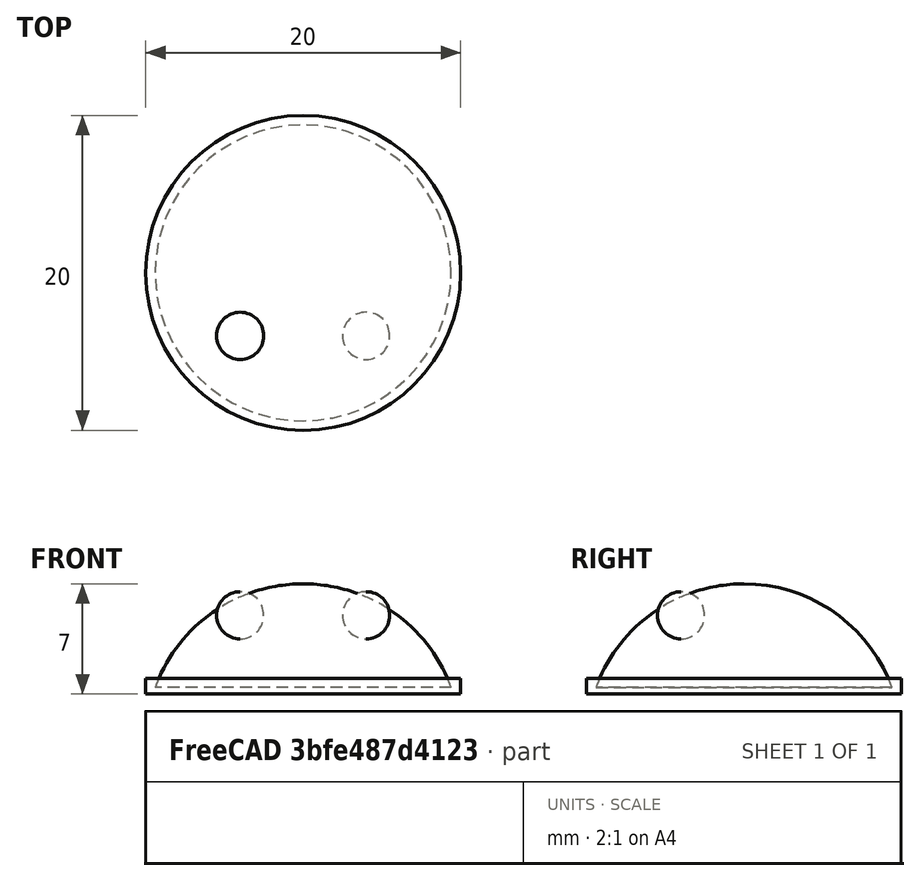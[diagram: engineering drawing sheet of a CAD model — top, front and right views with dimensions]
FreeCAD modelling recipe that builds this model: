
FCSTD DOCUMENT  (FreeCAD 0.21R33694 (Git))
Label: OJT1_T13R01_capderobot
License: All rights reserved
LicenseURL: https://en.wikipedia.org/wiki/All_rights_reserved
objects: Part::Sphere×3, Part::Cylinder×1
note: 4 computed .brp shape members not serialized (recipe doc carries the construction recipe); baked Part::Feature solids carry a one-line shape summary decoded from their .brp

FEATURE [Part::Cylinder] Cylinder  label="Cilindre"
  Angle = 360
  AttacherType = Attacher::AttachEngine3D
  FirstAngle = 0
  Height = 1
  Radius = 10
  SecondAngle = 0
FEATURE [Part::Sphere] Sphere  label="Esfera"
  Angle1 = 20
  Angle2 = 90
  Angle3 = 360
  AttacherType = Attacher::AttachEngine3D
  Placement = pos=(0,0,-3) rot=(0,0,1;0rad)
  Radius = 10
FEATURE [Part::Sphere] Sphere001  label="Ull_1"
  Angle1 = -90
  Angle2 = 90
  Angle3 = 360
  AttacherType = Attacher::AttachEngine3D
  Placement = pos=(4,-4,5) rot=(0,0,1;0rad)
  Radius = 1.5
FEATURE [Part::Sphere] Sphere002  label="Ull_2"
  Angle1 = -90
  Angle2 = 90
  Angle3 = 360
  AttacherType = Attacher::AttachEngine3D
  Placement = pos=(-4,-4,5) rot=(0,0,1;0rad)
  Radius = 1.5
